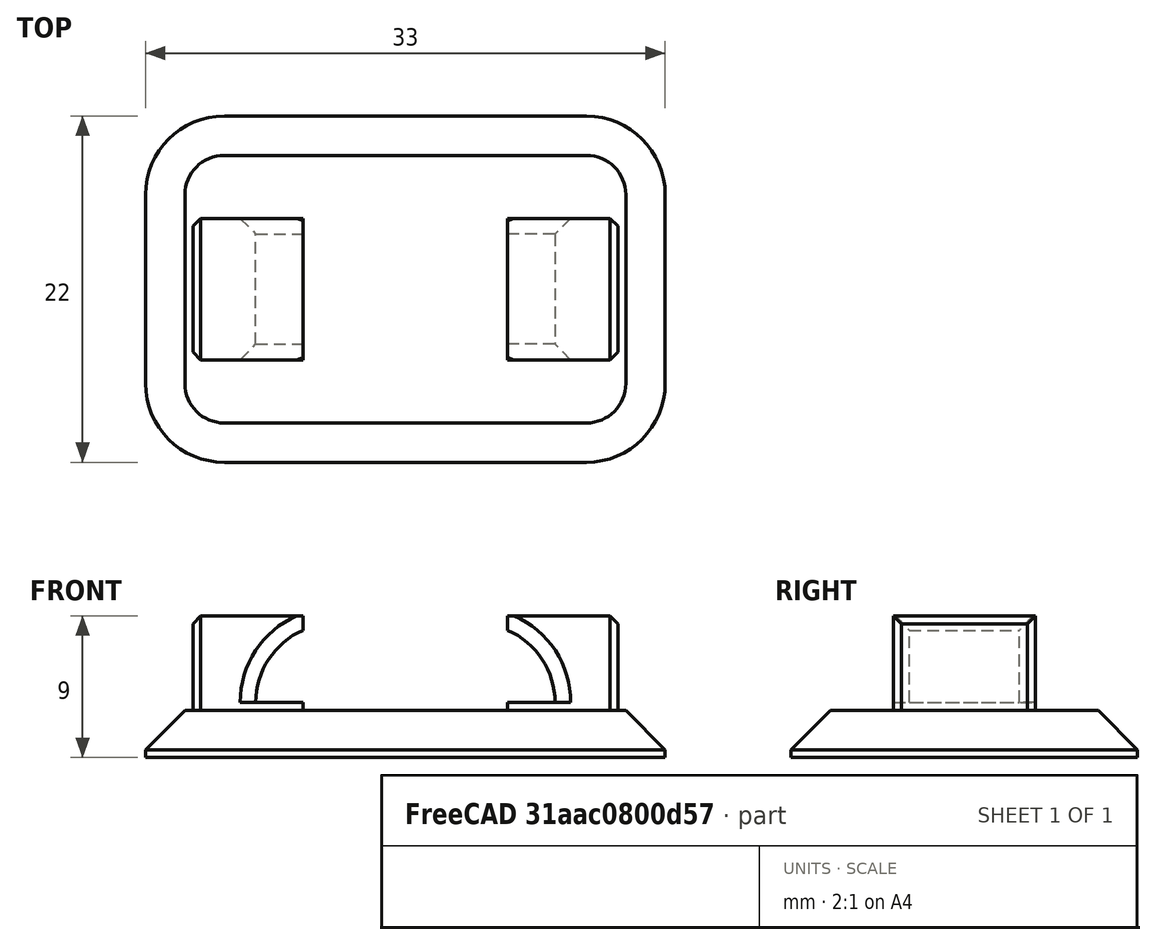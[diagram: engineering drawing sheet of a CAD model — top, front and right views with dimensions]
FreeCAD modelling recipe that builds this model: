
FCSTD DOCUMENT  (FreeCAD 0.18R4 (GitTag))
Label: gancho
License: All rights reserved
LicenseURL: http://en.wikipedia.org/wiki/All_rights_reserved
objects: PartDesign::Line×4, PartDesign::Chamfer×3, Sketcher::SketchObject×2, PartDesign::Pad×2, PartDesign::Body×2, Fem::ConstraintForce×2, PartDesign::Point×1, PartDesign::SubtractiveCylinder×1, PartDesign::FeatureBase×1, Part::MultiFuse×1, Fem::FemSolverObjectPython×1, Fem::ConstraintFixed×1, Fem::FemMeshShapeNetgenObject×1, App::MaterialObjectPython×1, Fem::FemAnalysis×1
note: 20 computed .brp shape members not serialized (recipe doc carries the construction recipe); baked Part::Feature solids carry a one-line shape summary decoded from their .brp

FEATURE [Sketcher::SketchObject] Sketch  label="BasePad"
  MapMode = 5
  Support = -> [XY_Plane]
  sketch-geometry (10):
    g0: ArcOfCircle CenterX=28 CenterY=17 CenterZ=0 NormalX=0 NormalY=0 NormalZ=1 AngleXU=0 Radius=5 StartAngle=0 EndAngle=1.5708
    g1: ArcOfCircle CenterX=5 CenterY=5 CenterZ=0 NormalX=0 NormalY=0 NormalZ=1 AngleXU=0 Radius=5 StartAngle=3.14159 EndAngle=4.71239
    g2: GeomPoint X=5 Y=17 Z=0
    g3: GeomPoint X=28 Y=5 Z=0
    g4: ArcOfCircle CenterX=5 CenterY=17 CenterZ=0 NormalX=0 NormalY=0 NormalZ=1 AngleXU=0 Radius=5 StartAngle=1.5708 EndAngle=3.14159
    g5: ArcOfCircle CenterX=28 CenterY=5 CenterZ=0 NormalX=0 NormalY=0 NormalZ=1 AngleXU=0 Radius=5 StartAngle=4.71239 EndAngle=6.28319
    g6: LineSegment StartX=5 StartY=22 StartZ=0 EndX=28 EndY=22 EndZ=0
    g7: LineSegment StartX=33 StartY=17 StartZ=0 EndX=33 EndY=5 EndZ=0
    g8: LineSegment StartX=28 StartY=-8e-16 StartZ=0 EndX=5 EndY=-7e-16 EndZ=0
    g9: LineSegment StartX=4e-16 StartY=5 StartZ=0 EndX=2e-16 EndY=17 EndZ=0
  constraints (28):
    c: Vertical(g0,g0)
    c: Horizontal(g0,g0)
    c: Radius(g0) = 5
    c: Horizontal(g1,g1)
    c: Vertical(g1,g1)
    c: Radius(g1) = 5
    c: Coincident(g4,g2)
    c: Coincident(g5,g3)
    c: Horizontal(g2,g4)
    c: Vertical(g2,g4)
    c: Coincident(g6,g4)
    c: Coincident(g6,g0)
    c: Horizontal(g6)
    c: Coincident(g7,g0)
    c: Vertical(g7)
    c: Coincident(g8,g5)
    c: Coincident(g8,g1)
    c: Coincident(g9,g1)
    c: Coincident(g9,g4)
    c: Radius(g4) = 5
    c: Radius(g5) = 5
    c: Coincident(g5,g7)
    c: Vertical(g3,g5)
    c: Horizontal(g5,g3)
    c: DistanceX(g4,g0) = 33
    c: DistanceY(g5,g0) = 22
    c: Tangent(g8,g-1)
    c: Tangent(g9,g-2)
FEATURE [PartDesign::Pad] Pad
  Length = 3
  Length2 = 100
  Profile = -> Sketch
  Type = 0
FEATURE [PartDesign::Chamfer] Chamfer
  Base = -> Pad [Edge19,Edge16,Edge13,Edge10,Edge7,Edge4,Edge24,Edge22]
  BaseFeature = -> Pad
  Size = 2.5
FEATURE [PartDesign::Line] DatumLine  label="BasePad_Top"
  AttacherType = Attacher::AttachEngineLine
  MapMode = 29
  Placement = pos=(0,22,0) rot=(0.57735,0.57735,0.57735;2.0944rad)
  Support = -> [Sketch]
FEATURE [PartDesign::Line] DatumLine001  label="BasePad_Bottom"
  AttacherType = Attacher::AttachEngineLine
  MapMode = 29
  Placement = pos=(0,-5e-16,0) rot=(-0.57735,0.57735,0.57735;4.18879rad)
  Support = -> [Sketch]
FEATURE [PartDesign::Line] DatumLine002  label="BasePad_Left"
  AttacherType = Attacher::AttachEngineLine
  MapMode = 29
  Placement = pos=(5e-16,0,0) rot=(0,0.707107,0.707107;3.14159rad)
  Support = -> [Sketch]
FEATURE [PartDesign::Point] DatumPoint
  AttacherType = Attacher::AttachEnginePoint
  AttachmentOffset = pos=(-10,0,0) rot=(0,0,1;0rad)
  MapMode = 37
  Placement = pos=(6.5,11,3) rot=(0,0,1;0rad)
  Support = -> [Pad]
FEATURE [PartDesign::Line] DatumLine004
  AttacherType = Attacher::AttachEngineLine
  MapMode = 17
  Placement = pos=(6.5,11,3) rot=(1,0,0;1.5708rad)
  Support = -> [DatumPoint]
FEATURE [Sketcher::SketchObject] Sketch001  label="HookAnchor"
  ExternalGeometry = -> [DatumLine004,DatumLine]
  MapMode = 5
  Placement = pos=(0,0,3) rot=(0,0,1;0rad)
  Support = -> [Pad]
  sketch-geometry (5):
    g0: LineSegment StartX=3 StartY=15.5 StartZ=0 EndX=10 EndY=15.5 EndZ=0
    g1: LineSegment StartX=10 StartY=15.5 StartZ=0 EndX=10 EndY=6.5 EndZ=0
    g2: LineSegment StartX=10 StartY=6.5 StartZ=0 EndX=3 EndY=6.5 EndZ=0
    g3: LineSegment StartX=3 StartY=6.5 StartZ=0 EndX=3 EndY=15.5 EndZ=0
    g4: GeomPoint X=6.5 Y=11 Z=0
  constraints (13):
    c: Coincident(g0,g1)
    c: Coincident(g1,g2)
    c: Coincident(g3,g0)
    c: Horizontal(g0)
    c: Vertical(g1)
    c: PointOnObject(g4,g-3)
    c: Distance(g4,g-4) = 11
    c: Equal(g2,g0)
    c: Equal(g1,g3)
    c: DistanceX(g0,g0) = 7
    c: DistanceY(g1,g1) = 9
    c: Symmetric(g2,g0,g4)
    c: Coincident(g3,g2)
FEATURE [PartDesign::Pad] Pad001
  BaseFeature = -> Chamfer
  Length = 6
  Length2 = 100
  Profile = -> Sketch001
  Type = 0
FEATURE [PartDesign::SubtractiveCylinder] Cylinder
  Angle = 90
  AttacherType = Attacher::AttachEngine3D
  AttachmentOffset = pos=(6.5,3.5,2) rot=(0,1,0;1.5708rad)
  BaseFeature = -> Pad001
  Height = 9
  MapMode = 5
  Placement = pos=(12,6.5,3.5) rot=(0,0.707107,0.707107;3.14159rad)
  Radius = 5
  Support = -> [Pad001]
FEATURE [PartDesign::Chamfer] Chamfer001
  Base = -> Cylinder [Edge50,Edge56]
  BaseFeature = -> Cylinder
  Placement = pos=(12,6.5,3.5) rot=(0,0.707107,0.707107;3.14159rad)
  Size = 1
FEATURE [PartDesign::Chamfer] Chamfer002
  Base = -> Chamfer001 [Edge10,Edge16,Edge3]
  BaseFeature = -> Chamfer001
  Placement = pos=(12,6.5,3.5) rot=(0,0.707107,0.707107;3.14159rad)
  Size = 0.5
FEATURE [PartDesign::Body] Body
  Group = -> [Sketch,Pad,Chamfer,DatumLine,DatumLine001,DatumLine002,DatumPoint,DatumLine004,Sketch001,Pad001,Cylinder,Chamfer001,Chamfer002]
  Origin = -> Origin
  Tip = -> Chamfer002
FEATURE [PartDesign::FeatureBase] Clone
  BaseFeature = -> Chamfer002
  Placement = pos=(12,6.5,3.5) rot=(0,0.707107,0.707107;3.14159rad)
FEATURE [PartDesign::Body] Body001
  BaseFeature = -> Chamfer002
  Group = -> [Clone]
  Origin = -> Origin001
  Placement = pos=(33,22,0) rot=(0,0,1;3.14159rad)
  Tip = -> Clone
FEATURE [Part::MultiFuse] Fusion
  Shapes = -> [Body,Body001]
FEATURE [Fem::FemSolverObjectPython] CalculiXccxTools  # FEM object (typed FeaturePython)
  AnalysisType = 1
  BeamShellResultOutput3D = false
  EigenmodeHighLimit = 1000000
  EigenmodeLowLimit = 0
  EigenmodesCount = 10
  GeometricalNonlinearity = 0
  IterationsControlParameterCutb = 0.25,0.5,0.75,0.85,,,1.5,
  IterationsControlParameterIter = 4,8,9,200,10,400,,200,,
  IterationsControlParameterTimeUse = false
  IterationsThermoMechMaximum = 200
  IterationsUserDefinedIncrementations = false
  IterationsUserDefinedTimeStepLength = false
  MaterialNonlinearity = 0
  MatrixSolverType = 0
  SplitInputWriter = false
  ThermoMechSteadyState = true
  TimeEnd = 1
  TimeInitialStep = 1
FEATURE [Fem::ConstraintFixed] FemConstraintFixed
  NormalDirection = (-1e-16,0,-1)
  Normals = (8) [(-8.65956e-17,-7.4988e-33,-1),(-8.65956e-17,-7.4988e-33,-1),(-8.65956e-17,-7.4988e-33,-1),(-8.65956e-17,-7.4988e-33,-1),(-8.65956e-17,-7.4988e-33,-1),+3 more]
  Points = (8) [(11,-1.77636e-15,-1.74417e-15),(22,-1.77636e-15,-2.69672e-15),(-1.06581e-14,11,-7.91619e-16),(11,11,-1.74417e-15),(22,11,-2.69672e-15),+3 more]
  References = -> [Fusion]
  Scale = 4
FEATURE [Fem::FemMeshShapeNetgenObject] FEMMeshNetgen
  Fineness = 1
  GrowthRate = 0.3
  MaxSize = 1000
  NbSegsPerEdge = 1
  NbSegsPerRadius = 2
  Optimize = true
  SecondOrder = false
  Shape = -> Fusion
FEATURE [Fem::ConstraintForce] FemConstraintForce
  Direction = -> Fusion [Face12]
  DirectionVector = (-1,-1e-16,1e-16)
  Force = 300
  NormalDirection = (0.83666,1e-16,-0.547723)
  Points = (9) [(7,7.5,3.5),(7.8167,7.5,6.23861),(10,7.5,8.08258),(7,11,3.5),(7.8167,11,6.23861),(10,11,8.08258),(7,14.5,3.5),(7.8167,14.5,6.23861),(10,14.5,8.08258)]
  References = -> [Fusion]
FEATURE [Fem::ConstraintForce] FemConstraintForce001
  Direction = -> Fusion [Face27]
  DirectionVector = (1,1e-16,1e-16)
  Force = 300
  NormalDirection = (-0.83666,1e-16,-0.547723)
  Points = (9) [(26,14.5,3.5),(25.1833,14.5,6.23861),(23,14.5,8.08258),(26,11,3.5),(25.1833,11,6.23861),(23,11,8.08258),(26,7.5,3.5),(25.1833,7.5,6.23861),+1 more]
  References = -> [Fusion]
FEATURE [App::MaterialObjectPython] SolidMaterial  # material (typed FeaturePython)
  Category = 0
  Material = Density=1240 kg/m^3,+12 more (map truncated)
FEATURE [Fem::FemAnalysis] Analysis
  Group = -> [CalculiXccxTools,FemConstraintFixed,FEMMeshNetgen,FemConstraintForce,FemConstraintForce001,SolidMaterial]
